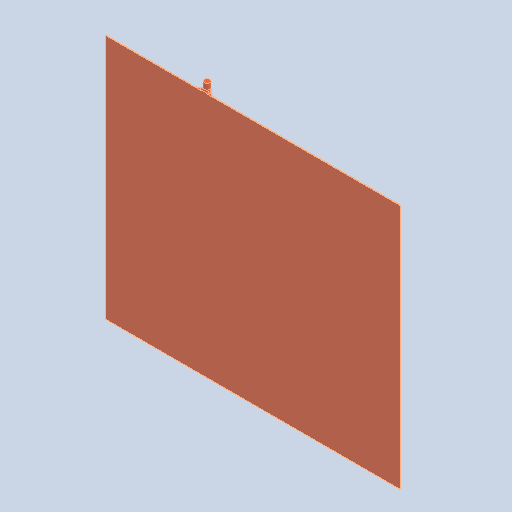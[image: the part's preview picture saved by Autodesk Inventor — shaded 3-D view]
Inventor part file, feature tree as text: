
AUTODESK INVENTOR PART (.ipt)
format: ipt  version: 2024 (Build 280153000, 153)  size: 267,776 bytes
history: native  units: mm
features: fillet x5, extrude x2, sketch x2
ambient origin geometry x8: Origin, YZ Plane, XZ Plane, XY Plane, X Axis, Y Axis, Z Axis, Center Point
bodies: Solid1 (feature_tree)
feature tree (9):
  extrude  "Extrusion1"  Depth=250.0mm
  fillet  "Fillet1"  Radius=1.0mm
  extrude  "Extrusion2"  Depth=6.0mm
  fillet  "Fillet3"  Radius=3.5mm
  fillet  "Fillet4"  Radius=50.0mm
  fillet  "Fillet5"  Radius=8.0mm
  fillet  "Fillet6"  Radius=3.0mm
  sketch  "Sketch1"  dims[d0=300.0mm d1=250.0mm d2=1.0mm d3=0.0mm]
  sketch  "Sketch2"  dims[d4=1.0mm d6=6.0mm d7=3.5mm d8=50.0mm d9=8.0mm d10=30.0mm d11=0.0mm d12=0.0mm d13=3.0mm d14=10.0mm d15=2.0mm d16=0.5mm]
